# Revit family: 201_KIR4
name_source: partatom
category: Air Terminals
revit_build: Autodesk Revit 2018 (Build: 20170223_1515(x64)
units: mm (PartAtom-declared; Revit-internal decimal feet)

## family parameters
Always vertical = Yes
Cut with Voids When Loaded = No
Part Type = Normal
Room Calculation Point = Yes
Round Connector Dimension = Use Diameter
Shared = No
Work Plane-Based = No

## types (2) — shared parameters
CAT0 = Yes
CL_Location_5000 = 5000 mm  [stored 16.4042 ft]
Description = Supply valve steel white
H3 = 13 mm  [stored 0.0426509 ft]
L_ARR = 400 mm  [stored 1.31234 ft]
Manufacturer = Flexit
QmdConnectorList = 201;D
R = 2 mm  [stored 0.00656168 ft]
URL = www.flexit.no
W_ARR = 400 mm  [stored 1.31234 ft]
Z2 = 18 mm  [stored 0.0590551 ft]
Z3 = 7 mm  [stored 0.0229659 ft]
magiPartTypeId = 201
magiProductFamilyId = KIR4
zero-valued in all types: CLBTZ, H_ARR

## per-type parameters (varying)
| type | D | D2 | D3 | R2 | magiProductId |
| 100-116775 | 100 mm | 120 mm | 135 mm | 55 mm  [stored 0.180446 ft] | KIR 1004 |
| 125-116776 | 125 mm | 145 mm  [stored 0.475722 ft] | 165 mm  [stored 0.541339 ft] | 68 mm | KIR 1254 |

note: column(s) folded — value = type name in every type: MC Product Code

note: [stored X ft] marks values corroborated as IEEE doubles in the binary element streams (Revit-internal decimal feet)

## geometry (parser evidence)
native form markers: Sweep x1
no freeform markers — native parametric forms only
